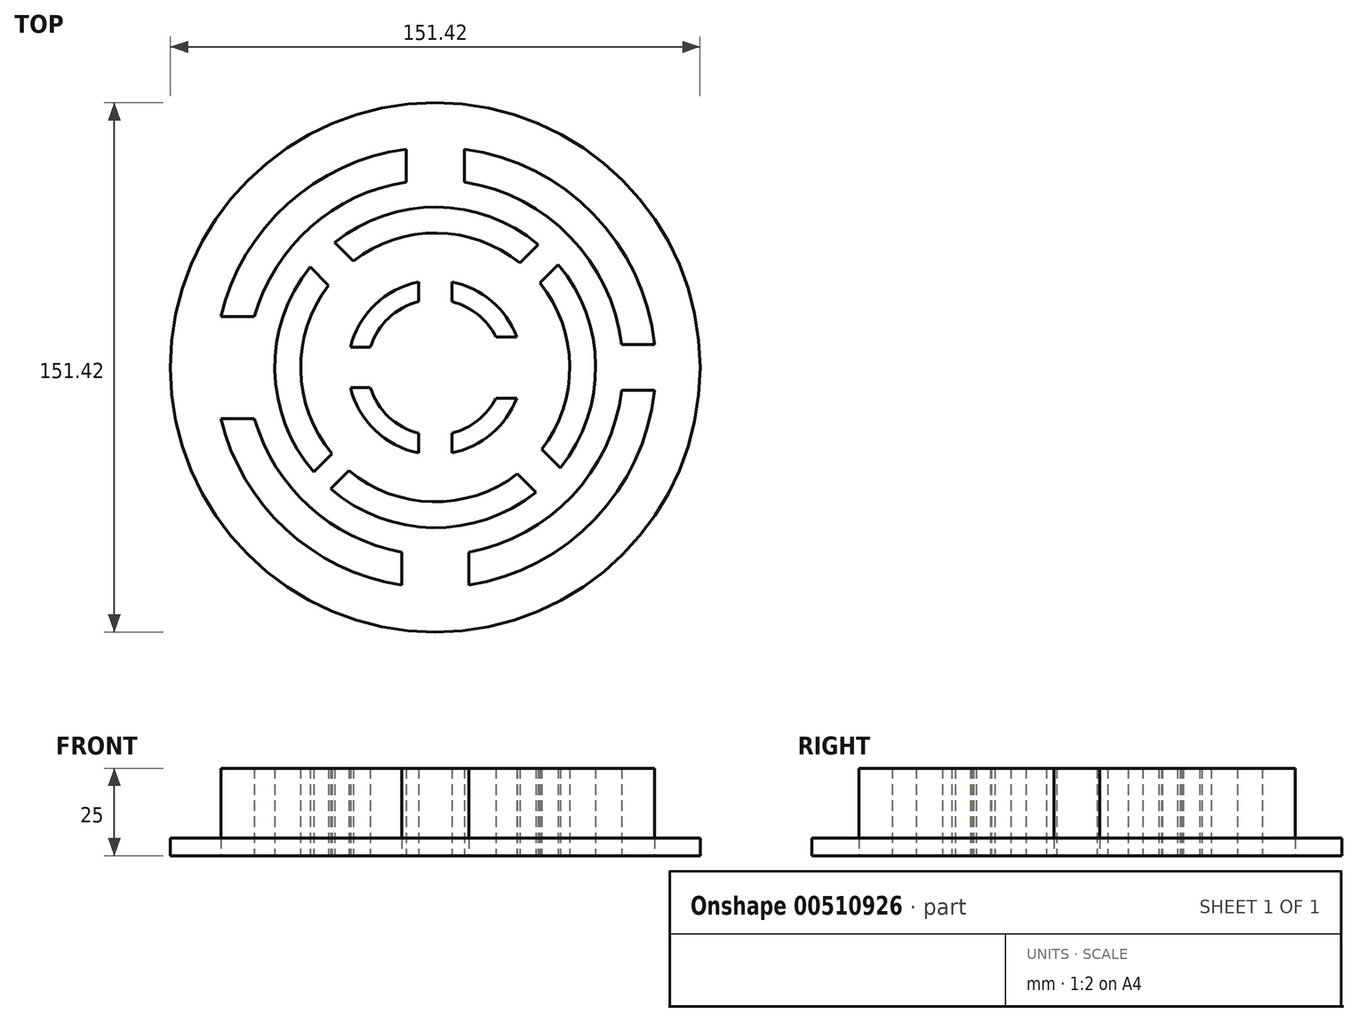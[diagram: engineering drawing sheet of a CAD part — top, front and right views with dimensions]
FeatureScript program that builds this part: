
annotation { "Feature Type Name" : "Feature", "Feature Type Description" : "" }
export const myFeature = defineFeature(function(context is Context, id is Id, definition is map)
    precondition{}
    {
        {
            var Q0;
            Q0=qCreatedBy(makeId("Top.planeOp"),FACE);
            var sketch = newSketch(context, id + "F0", { "sketchPlane" : qUnion([Q0])});
            skCircle(sketch, "E0", {"center": v(0, 0) * mm, "radius": 75.71 * mm});
            skSolve(sketch);
        }
        {
            var Q0;
            Q0 = qSketchRegion(id + "F0", true);
            extrude(context, id + "F1", {"entities" : qUnion([Q0]), "depth" : 5 * mm});
        }
        {
            var Q0;
            Q0=qCreatedBy(makeId("Top.planeOp"),FACE);
            var sketch = newSketch(context, id + "F2", { "sketchPlane" : qUnion([Q0])});
            skArc(sketch, "E1", {"start": v(-4.77, 18.82) * mm, "mid": v(-13.35, 14.1) * mm, "end": v(-18.54, 5.78) * mm});
            skArc(sketch, "E2", {"start": v(-18.54, -5.78) * mm, "mid": v(-13.35, -14.1) * mm, "end": v(-4.77, -18.82) * mm});
            skArc(sketch, "E3", {"start": v(17.32, 8.76) * mm, "mid": v(12.14, 15.15) * mm, "end": v(4.77, 18.82) * mm});
            skArc(sketch, "E4", {"start": v(4.77, -18.82) * mm, "mid": v(12.14, -15.15) * mm, "end": v(17.32, -8.76) * mm});
            skArc(sketch, "E5", {"start": v(-4.77, 24.44) * mm, "mid": v(-17.24, 17.97) * mm, "end": v(-24.23, 5.78) * mm});
            skArc(sketch, "E6", {"start": v(23.31, 8.76) * mm, "mid": v(16.08, 19.02) * mm, "end": v(4.77, 24.44) * mm});
            skArc(sketch, "E7", {"start": v(4.77, -24.44) * mm, "mid": v(16.08, -19.02) * mm, "end": v(23.31, -8.76) * mm});
            skArc(sketch, "E8", {"start": v(-24.23, -5.78) * mm, "mid": v(-17.24, -17.97) * mm, "end": v(-4.77, -24.44) * mm});
            skArc(sketch, "E9", {"start": v(-4.95, 38.14) * mm, "mid": v(-27.74, 26.65) * mm, "end": v(-38.31, 3.42) * mm});
            skArc(sketch, "E10", {"start": v(38.25, 4.02) * mm, "mid": v(27.52, 26.87) * mm, "end": v(4.95, 38.14) * mm});
            skArc(sketch, "E11", {"start": v(-38.31, -3.42) * mm, "mid": v(-27.74, -26.65) * mm, "end": v(-4.95, -38.14) * mm});
            skArc(sketch, "E12", {"start": v(4.95, -38.14) * mm, "mid": v(27.52, -26.87) * mm, "end": v(38.25, -4.02) * mm});
            skArc(sketch, "E13", {"start": v(45.68, 4.02) * mm, "mid": v(32.76, 32.1) * mm, "end": v(4.95, 45.6) * mm});
            skArc(sketch, "E14", {"start": v(4.95, -45.6) * mm, "mid": v(32.76, -32.1) * mm, "end": v(45.68, -4.02) * mm});
            skArc(sketch, "E15", {"start": v(-45.73, -3.42) * mm, "mid": v(-32.97, -31.88) * mm, "end": v(-4.95, -45.6) * mm});
            skArc(sketch, "E16", {"start": v(-4.95, 45.6) * mm, "mid": v(-32.97, 31.88) * mm, "end": v(-45.73, 3.42) * mm});
            skLineSegment(sketch, "E17", {"start": v(-24.23, 5.78) * mm, "end": v(-18.54, 5.78) * mm});
            skLineSegment(sketch, "E18", {"start": v(-24.23, -5.78) * mm, "end": v(-18.54, -5.78) * mm});
            skLineSegment(sketch, "E19", {"start": v(17.32, 8.76) * mm, "end": v(23.31, 8.76) * mm});
            skLineSegment(sketch, "E20", {"start": v(17.32, -8.76) * mm, "end": v(23.31, -8.76) * mm});
            skLineSegment(sketch, "E21", {"start": v(-4.77, 24.44) * mm, "end": v(-4.77, 18.82) * mm});
            skLineSegment(sketch, "E22", {"start": v(4.77, 24.44) * mm, "end": v(4.77, 18.82) * mm});
            skLineSegment(sketch, "E23", {"start": v(-4.77, -18.82) * mm, "end": v(-4.77, -24.44) * mm});
            skLineSegment(sketch, "E24", {"start": v(4.77, -18.82) * mm, "end": v(4.77, -24.44) * mm});
            skLineSegment(sketch, "E25", {"start": v(-45.73, 3.42) * mm, "end": v(-38.31, 3.42) * mm});
            skLineSegment(sketch, "E26", {"start": v(-4.95, 45.6) * mm, "end": v(-4.95, 38.14) * mm});
            skLineSegment(sketch, "E27", {"start": v(4.95, 45.6) * mm, "end": v(4.95, 38.14) * mm});
            skLineSegment(sketch, "E28", {"start": v(38.25, 4.02) * mm, "end": v(45.68, 4.02) * mm});
            skLineSegment(sketch, "E29", {"start": v(38.25, -4.02) * mm, "end": v(45.68, -4.02) * mm});
            skLineSegment(sketch, "E30", {"start": v(-4.95, -38.14) * mm, "end": v(-4.95, -45.6) * mm});
            skLineSegment(sketch, "E31", {"start": v(4.95, -38.14) * mm, "end": v(4.95, -45.6) * mm});
            skLineSegment(sketch, "E32", {"start": v(-45.73, -3.42) * mm, "end": v(-38.31, -3.42) * mm});
            skArc(sketch, "E33", {"start": v(9.62, -52.84) * mm, "mid": v(39.08, -36.85) * mm, "end": v(53.31, -6.5) * mm});
            skArc(sketch, "E34", {"start": v(9.62, -62.27) * mm, "mid": v(45.65, -43.43) * mm, "end": v(62.67, -6.5) * mm});
            skArc(sketch, "E35", {"start": v(-51.68, -14.6) * mm, "mid": v(-36.13, -39.74) * mm, "end": v(-9.62, -52.84) * mm});
            skArc(sketch, "E36", {"start": v(-61.3, -14.6) * mm, "mid": v(-42.72, -46.31) * mm, "end": v(-9.62, -62.27) * mm});
            skArc(sketch, "E37", {"start": v(-8.28, 53.07) * mm, "mid": v(-35.62, 40.2) * mm, "end": v(-51.68, 14.6) * mm});
            skArc(sketch, "E38", {"start": v(-8.28, 62.46) * mm, "mid": v(-42.22, 46.77) * mm, "end": v(-61.3, 14.6) * mm});
            skArc(sketch, "E39", {"start": v(53.31, 6.5) * mm, "mid": v(38.6, 37.34) * mm, "end": v(8.28, 53.07) * mm});
            skArc(sketch, "E40", {"start": v(62.67, 6.5) * mm, "mid": v(45.18, 43.92) * mm, "end": v(8.28, 62.46) * mm});
            skLineSegment(sketch, "E41", {"start": v(8.28, 62.46) * mm, "end": v(8.28, 53.07) * mm});
            skLineSegment(sketch, "E42", {"start": v(62.67, 6.5) * mm, "end": v(53.31, 6.5) * mm});
            skLineSegment(sketch, "E43", {"start": v(62.67, -6.5) * mm, "end": v(53.31, -6.5) * mm});
            skLineSegment(sketch, "E44", {"start": v(9.62, -52.84) * mm, "end": v(9.62, -62.27) * mm});
            skLineSegment(sketch, "E45", {"start": v(-9.62, -52.84) * mm, "end": v(-9.62, -62.27) * mm});
            skLineSegment(sketch, "E46", {"start": v(-51.68, -14.6) * mm, "end": v(-61.3, -14.6) * mm});
            skLineSegment(sketch, "E47", {"start": v(-51.68, 14.6) * mm, "end": v(-61.3, 14.6) * mm});
            skLineSegment(sketch, "E48", {"start": v(-8.28, 62.46) * mm, "end": v(-8.28, 53.07) * mm});
            skSolve(sketch);
        }
        {
            var Q0;
            Q0 = qSketchRegion(id + "F2", true);
            extrude(context, id + "F3", {"entities" : qUnion([Q0]), "depth" : 25 * mm});
        }
        {
            var Q0;
            Q0=makeQuery(id+"F3.opExtrude","SWEPT_BODY",BODY,{"disambiguationData":[OSD([sQuery(id+"F2.wireOp",EDGE,"E9"),sQuery(id+"F2.wireOp",EDGE,"E16"),sQuery(id+"F2.wireOp",EDGE,"E25"),sQuery(id+"F2.wireOp",EDGE,"E26")])]});
            var Q1;
            Q1=makeQuery(id+"F3.opExtrude","SWEPT_BODY",BODY,{"disambiguationData":[OSD([sQuery(id+"F2.wireOp",EDGE,"E11"),sQuery(id+"F2.wireOp",EDGE,"E15"),sQuery(id+"F2.wireOp",EDGE,"E30"),sQuery(id+"F2.wireOp",EDGE,"E32")])]});
            var Q2;
            Q2=makeQuery(id+"F3.opExtrude","SWEPT_BODY",BODY,{"disambiguationData":[OSD([sQuery(id+"F2.wireOp",EDGE,"E12"),sQuery(id+"F2.wireOp",EDGE,"E14"),sQuery(id+"F2.wireOp",EDGE,"E29"),sQuery(id+"F2.wireOp",EDGE,"E31")])]});
            var Q3;
            Q3=makeQuery(id+"F3.opExtrude","SWEPT_BODY",BODY,{"disambiguationData":[OSD([sQuery(id+"F2.wireOp",EDGE,"E10"),sQuery(id+"F2.wireOp",EDGE,"E13"),sQuery(id+"F2.wireOp",EDGE,"E27"),sQuery(id+"F2.wireOp",EDGE,"E28")])]});
            var Q4;
            Q4=makeQuery(id+"F3.opExtrude","SWEPT_FACE",FACE,{"disambiguationData":[OSD([sQuery(id+"F2.wireOp",EDGE,"E1")])]});
            transform(context, id + "F4", {"entities" : qUnion([Q0, Q1, Q2, Q3]), "transformType" : TransformType.ROTATION, "transformAxis" : qUnion([Q4]), "angle" : 45 * degree, "makeCopy" : false});
        }
    });
